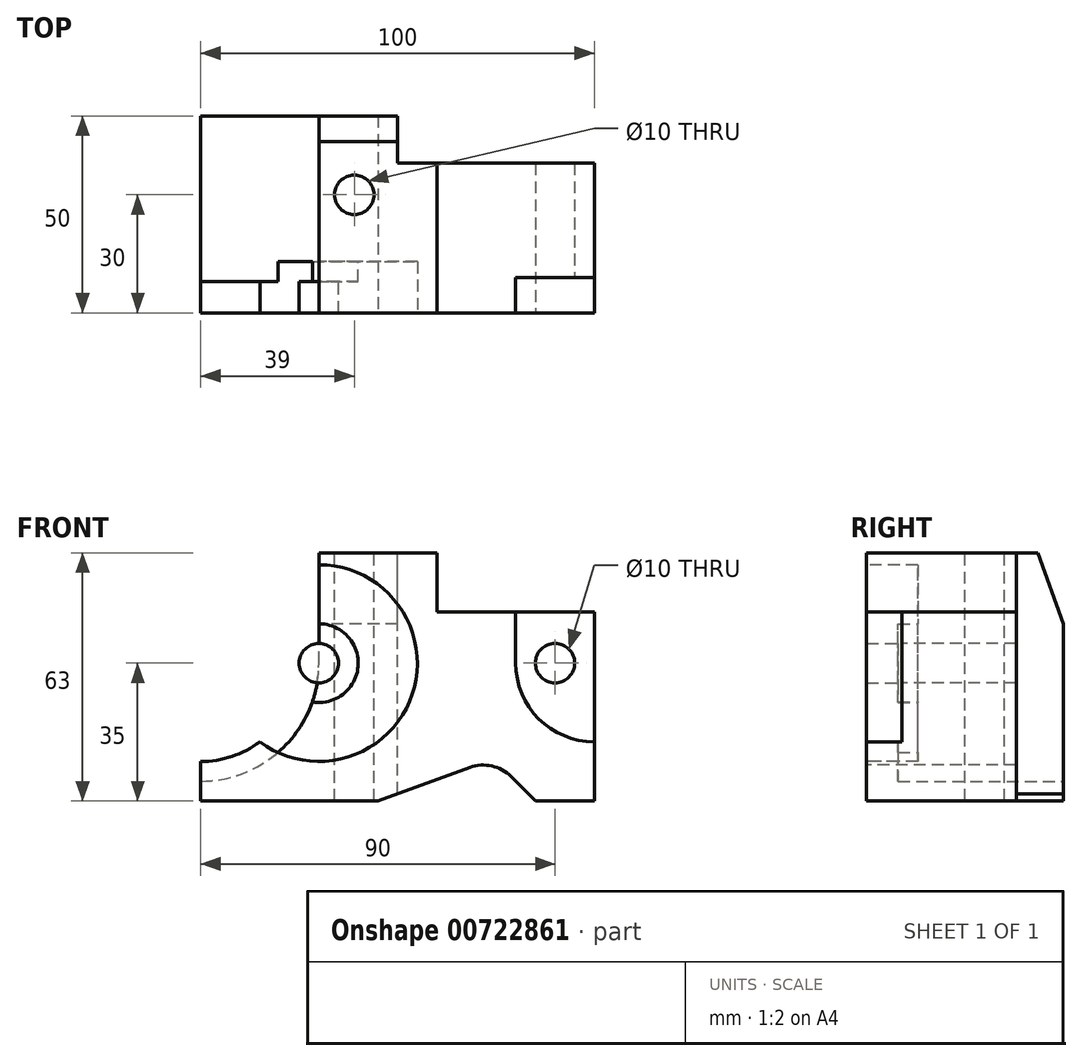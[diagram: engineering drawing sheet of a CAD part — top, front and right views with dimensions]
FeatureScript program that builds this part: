
annotation { "Feature Type Name" : "Feature", "Feature Type Description" : "" }
export const myFeature = defineFeature(function(context is Context, id is Id, definition is map)
    precondition{}
    {
        {
            var Q0;
            Q0=qCreatedBy(makeId("Front.planeOp"),FACE);
            var sketch = newSketch(context, id + "F0", { "sketchPlane" : qUnion([Q0])});
            skLineSegment(sketch, "E0", {"start": v(0, 0) * mm, "end": v(0, 63) * mm});
            skLineSegment(sketch, "E1", {"start": v(0, 0) * mm, "end": v(100, 0) * mm, "construction": true});
            skLineSegment(sketch, "E2", {"start": v(100, 0) * mm, "end": v(85, 0) * mm});
            skLineSegment(sketch, "E3", {"start": v(0, 0) * mm, "end": v(45, 0) * mm});
            skLineSegment(sketch, "E4", {"start": v(45, 0) * mm, "end": v(68.34, 8.5) * mm});
            skLineSegment(sketch, "E5", {"start": v(85, 0) * mm, "end": v(78.83, 6.17) * mm});
            skArc(sketch, "E6", {"start": v(78.83, 6.17) * mm, "mid": v(73.92, 8.86) * mm, "end": v(68.34, 8.5) * mm});
            skLineSegment(sketch, "E7", {"start": v(0, 63) * mm, "end": v(60, 63) * mm});
            skLineSegment(sketch, "E8", {"start": v(60, 63) * mm, "end": v(60, 48) * mm});
            skLineSegment(sketch, "E9", {"start": v(60, 48) * mm, "end": v(100, 48) * mm});
            skLineSegment(sketch, "E10", {"start": v(100, 48) * mm, "end": v(100, 0) * mm});
            skLineSegment(sketch, "E11", {"start": v(0, 35) * mm, "end": v(100, 35) * mm, "construction": true});
            skSolve(sketch);
        }
        {
            var Q0;
            Q0 = qSketchRegion(id + "F0", true);
            extrude(context, id + "F1", {"entities" : qUnion([Q0]), "oppositeDirection" : true, "depth" : 50 * mm, "offsetDistance" : 25 * mm});
        }
        {
            var Q0;
            Q0=makeQuery(id+"F1.opExtrude","CAP_FACE",FACE,{"disambiguationData":[OSD([sQuery(id+"F0.wireOp",EDGE,"E0"),sQuery(id+"F0.wireOp",EDGE,"E2"),sQuery(id+"F0.wireOp",EDGE,"E3"),sQuery(id+"F0.wireOp",EDGE,"E4"),sQuery(id+"F0.wireOp",EDGE,"E5"),sQuery(id+"F0.wireOp",EDGE,"E6"),sQuery(id+"F0.wireOp",EDGE,"E7"),sQuery(id+"F0.wireOp",EDGE,"E8"),sQuery(id+"F0.wireOp",EDGE,"E9"),sQuery(id+"F0.wireOp",EDGE,"E10")])],"isStart":true});
            var sketch = newSketch(context, id + "F2", { "sketchPlane" : qUnion([Q0])});
            skArc(sketch, "E12", {"start": v(80, 35) * mm, "mid": v(85.86, 20.86) * mm, "end": v(100, 15) * mm});
            skLineSegment(sketch, "E13", {"start": v(80, 35) * mm, "end": v(80, 48) * mm});
            skPoint(sketch, "E13.startSnap0", {"position": v(80, 48) * mm});
            skLineSegment(sketch, "E14", {"start": v(80, 48) * mm, "end": v(100, 48) * mm});
            skLineSegment(sketch, "E15", {"start": v(100, 48) * mm, "end": v(100, 15) * mm});
            skSolve(sketch);
        }
        {
            var Q0;
            Q0 = qSketchRegion(id + "F2", true);
            extrude(context, id + "F3", {"entities" : qUnion([Q0]), "operationType" : NewBodyOperationType.REMOVE, "oppositeDirection" : true, "depth" : 9 * mm, "offsetDistance" : 25 * mm});
        }
        {
            var Q0;
            Q0=makeQuery(id+"F3.boolean.opBoolean","COPY",FACE,{"derivedFrom":makeQuery(id+"F3.opExtrude","CAP_FACE",FACE,{"disambiguationData":[OSD([sQuery(id+"F2.wireOp",EDGE,"E12"),sQuery(id+"F2.wireOp",EDGE,"E13"),sQuery(id+"F2.wireOp",EDGE,"E14"),sQuery(id+"F2.wireOp",EDGE,"E15")])],"isStart":false})});
            var sketch = newSketch(context, id + "F4", { "sketchPlane" : qUnion([Q0])});
            skCircle(sketch, "E16", {"center": v(90, 35) * mm, "radius": 5 * mm});
            skSolve(sketch);
        }
        {
            var Q0;
            Q0 = qSketchRegion(id + "F4", true);
            extrude(context, id + "F5", {"entities" : qUnion([Q0]), "operationType" : NewBodyOperationType.REMOVE, "endBound" : BoundingType.THROUGH_ALL, "oppositeDirection" : true, "depth" : 25 * mm, "offsetDistance" : 25 * mm});
        }
        {
            var Q0;
            Q0=makeQuery(id+"F1.opExtrude","CAP_FACE",FACE,{"disambiguationData":[OSD([sQuery(id+"F0.wireOp",EDGE,"E0"),sQuery(id+"F0.wireOp",EDGE,"E2"),sQuery(id+"F0.wireOp",EDGE,"E3"),sQuery(id+"F0.wireOp",EDGE,"E4"),sQuery(id+"F0.wireOp",EDGE,"E5"),sQuery(id+"F0.wireOp",EDGE,"E6"),sQuery(id+"F0.wireOp",EDGE,"E7"),sQuery(id+"F0.wireOp",EDGE,"E8"),sQuery(id+"F0.wireOp",EDGE,"E9"),sQuery(id+"F0.wireOp",EDGE,"E10")])],"isStart":true});
            var sketch = newSketch(context, id + "F6", { "sketchPlane" : qUnion([Q0])});
            skLineSegment(sketch, "E17", {"start": v(0, 35) * mm, "end": v(80, 35) * mm, "construction": true});
            skCircle(sketch, "E18", {"center": v(30, 35) * mm, "radius": 25 * mm});
            skSolve(sketch);
        }
        {
            var Q0;
            Q0 = qSketchRegion(id + "F6", true);
            extrude(context, id + "F7", {"entities" : qUnion([Q0]), "operationType" : NewBodyOperationType.REMOVE, "oppositeDirection" : true, "depth" : 13 * mm, "offsetDistance" : 25 * mm});
        }
        {
            var Q0;
            Q0=makeQuery(id+"F7.boolean.opBoolean","COPY",FACE,{"derivedFrom":makeQuery(id+"F7.opExtrude","CAP_FACE",FACE,{"disambiguationData":[OSD([sQuery(id+"F6.wireOp",EDGE,"E18")])],"isStart":false})});
            var sketch = newSketch(context, id + "F8", { "sketchPlane" : qUnion([Q0])});
            skCircle(sketch, "E19", {"center": v(30, 35) * mm, "radius": 10 * mm});
            skSolve(sketch);
        }
        {
            var Q0;
            Q0 = qSketchRegion(id + "F8", true);
            extrude(context, id + "F9", {"entities" : qUnion([Q0]), "operationType" : NewBodyOperationType.ADD, "depth" : 5 * mm, "offsetDistance" : 25 * mm});
        }
        {
            var Q0;
            Q0=makeQuery(id+"F9.opExtrude","CAP_FACE",FACE,{"disambiguationData":[OSD([sQuery(id+"F8.wireOp",EDGE,"E19")])],"isStart":false});
            var sketch = newSketch(context, id + "F10", { "sketchPlane" : qUnion([Q0])});
            skCircle(sketch, "E20", {"center": v(30, 35) * mm, "radius": 5 * mm});
            skSolve(sketch);
        }
        {
            var Q0;
            Q0 = qSketchRegion(id + "F10", true);
            extrude(context, id + "F11", {"entities" : qUnion([Q0]), "operationType" : NewBodyOperationType.ADD, "depth" : 8 * mm, "offsetDistance" : 25 * mm});
        }
        {
            var Q0;
            Q0=makeQuery(id+"F1.opExtrude","CAP_FACE",FACE,{"disambiguationData":[OSD([sQuery(id+"F0.wireOp",EDGE,"E0"),sQuery(id+"F0.wireOp",EDGE,"E2"),sQuery(id+"F0.wireOp",EDGE,"E3"),sQuery(id+"F0.wireOp",EDGE,"E4"),sQuery(id+"F0.wireOp",EDGE,"E5"),sQuery(id+"F0.wireOp",EDGE,"E6"),sQuery(id+"F0.wireOp",EDGE,"E7"),sQuery(id+"F0.wireOp",EDGE,"E8"),sQuery(id+"F0.wireOp",EDGE,"E9"),sQuery(id+"F0.wireOp",EDGE,"E10")])],"isStart":true});
            var sketch = newSketch(context, id + "F12", { "sketchPlane" : qUnion([Q0])});
            skCircle(sketch, "E21", {"center": v(0, 35) * mm, "radius": 25 * mm});
            skSolve(sketch);
        }
        {
            var Q0;
            Q0 = qSketchRegion(id + "F12", true);
            extrude(context, id + "F13", {"entities" : qUnion([Q0]), "operationType" : NewBodyOperationType.REMOVE, "endBound" : BoundingType.THROUGH_ALL, "oppositeDirection" : true, "depth" : 25 * mm, "offsetDistance" : 25 * mm});
        }
        {
            var Q0;
            Q0=makeQuery(id+"F1.opExtrude","CAP_FACE",FACE,{"disambiguationData":[OSD([sQuery(id+"F0.wireOp",EDGE,"E0"),sQuery(id+"F0.wireOp",EDGE,"E2"),sQuery(id+"F0.wireOp",EDGE,"E3"),sQuery(id+"F0.wireOp",EDGE,"E4"),sQuery(id+"F0.wireOp",EDGE,"E5"),sQuery(id+"F0.wireOp",EDGE,"E6"),sQuery(id+"F0.wireOp",EDGE,"E7"),sQuery(id+"F0.wireOp",EDGE,"E8"),sQuery(id+"F0.wireOp",EDGE,"E9"),sQuery(id+"F0.wireOp",EDGE,"E10")])],"isStart":false});
            var sketch = newSketch(context, id + "F14", { "sketchPlane" : qUnion([Q0])});
            skLineSegment(sketch, "E22", {"start": v(0, 0) * mm, "end": v(0, 63) * mm, "construction": true});
            skLineSegment(sketch, "E23", {"start": v(0, 35) * mm, "end": v(-100, 35) * mm, "construction": true});
            skPoint(sketch, "E24.startSnap0", {"position": v(-30, 63) * mm});
            skArc(sketch, "E25", {"start": v(-30, 35) * mm, "mid": v(-21.21, 13.79) * mm, "end": v(0, 5) * mm});
            skLineSegment(sketch, "E26", {"start": v(-30, 35) * mm, "end": v(-30, 63) * mm});
            skLineSegment(sketch, "E27", {"start": v(0, 5) * mm, "end": v(0, 63) * mm});
            skLineSegment(sketch, "E28", {"start": v(0, 63) * mm, "end": v(-30, 63) * mm});
            skSolve(sketch);
        }
        {
            var Q0;
            Q0 = qSketchRegion(id + "F14", true);
            extrude(context, id + "F15", {"entities" : qUnion([Q0]), "operationType" : NewBodyOperationType.REMOVE, "oppositeDirection" : true, "depth" : 42 * mm, "offsetDistance" : 25 * mm});
        }
        {
            var Q0;
            {var subQ0=sQuery(id+"F14.wireOp",EDGE,"E26");Q0=makeQuery(id+"F15.boolean.opBoolean","COPY",FACE,{"disambiguationData":[TD([makeQuery(id+"F1.opExtrude","SWEPT_FACE",FACE,{"disambiguationData":[OSD([sQuery(id+"F0.wireOp",EDGE,"E0")])]}),makeQuery(id+"F1.opExtrude","SWEPT_FACE",FACE,{"disambiguationData":[OSD([sQuery(id+"F0.wireOp",EDGE,"E7")])]}),makeQuery(id+"F7.boolean.opBoolean","COPY",FACE,{"derivedFrom":makeQuery(id+"F7.opExtrude","SWEPT_FACE",FACE,{"disambiguationData":[OSD([sQuery(id+"F6.wireOp",EDGE,"E18")])]})}),makeQuery(id+"F13.boolean.opBoolean","COPY",FACE,{"derivedFrom":makeQuery(id+"F13.opExtrude","SWEPT_FACE",FACE,{"disambiguationData":[OSD([sQuery(id+"F12.wireOp",EDGE,"E21")])]})}),makeQuery(id+"F15.opExtrude","SWEPT_FACE",FACE,{"disambiguationData":[OSD([subQ0])]})])],"derivedFrom":makeQuery(id+"F15.opExtrude","CAP_FACE",FACE,{"disambiguationData":[OSD([sQuery(id+"F14.wireOp",EDGE,"E25"),subQ0,sQuery(id+"F14.wireOp",EDGE,"E27"),sQuery(id+"F14.wireOp",EDGE,"E28")])],"isStart":false})});}
            var sketch = newSketch(context, id + "F16", { "sketchPlane" : qUnion([Q0])});
            skLineSegment(sketch, "E29", {"start": v(-30, 63) * mm, "end": v(-30, 60) * mm});
            skSolve(sketch);
        }
        {
            var Q0;
            Q0 = qSketchRegion(id + "F16", true);
            var Q1;
            Q1=makeQuery(id+"F16.imprint","IMPRINT",FACE,{"disambiguationData":[TD([[makeQuery(id+"F16.imprint","IMPRINT",EDGE,{"derivedFrom":sQuery(id+"F16.wireOp",EDGE,"E29")}),-1.0]])]});
            extrude(context, id + "F17", {"entities" : qUnion([Q0, Q1]), "operationType" : NewBodyOperationType.REMOVE, "endBound" : BoundingType.THROUGH_ALL, "oppositeDirection" : true, "depth" : 25 * mm, "offsetDistance" : 25 * mm});
        }
        {
            var Q0;
            Q0=makeQuery(id+"F1.opExtrude","SWEPT_FACE",FACE,{"disambiguationData":[OSD([sQuery(id+"F0.wireOp",EDGE,"E3")])]});
            cPlane(context, id + "F18", {"entities" : qUnion([Q0]), "cplaneType" : CPlaneType.OFFSET, "offset" : 63 * mm, "oppositeDirection" : true, "width" : 150 * mm, "height" : 150 * mm});
        }
        {
            var Q0;
            Q0=qCreatedBy(id+"F18.planeOp",FACE);
            var sketch = newSketch(context, id + "F19", { "sketchPlane" : qUnion([Q0])});
            skLineSegment(sketch, "E30.0.3", {"start": v(60, -50) * mm, "end": v(50, -50) * mm});
            skLineSegment(sketch, "E31.0.2", {"start": v(100, -38) * mm, "end": v(100, -50) * mm});
            skLineSegment(sketch, "E31.0.3", {"start": v(100, -50) * mm, "end": v(60, -50) * mm});
            skLineSegment(sketch, "E32", {"start": v(50, -50) * mm, "end": v(50, -38) * mm});
            skLineSegment(sketch, "E33", {"start": v(50, -38) * mm, "end": v(100, -38) * mm});
            skPoint(sketch, "E31.0.1.end.orphan", {"position": v(100, -9) * mm});
            skPoint(sketch, "E31.0.0.end.orphan", {"position": v(80, -9) * mm});
            skPoint(sketch, "E31.0.5.end.orphan", {"position": v(80, 0) * mm});
            skPoint(sketch, "E34.orphan", {"position": v(60, 0) * mm});
            skPoint(sketch, "E30.0.0.end.orphan", {"position": v(30, 0) * mm});
            skPoint(sketch, "E35.orphan", {"position": v(30, -50) * mm});
            skSolve(sketch);
        }
        {
            var Q0;
            Q0 = qSketchRegion(id + "F19", true);
            extrude(context, id + "F20", {"entities" : qUnion([Q0]), "operationType" : NewBodyOperationType.REMOVE, "endBound" : BoundingType.THROUGH_ALL, "depth" : 25 * mm, "offsetDistance" : 25 * mm});
        }
        {
            var Q0;
            Q0=makeQuery(id+"F17.boolean.opBoolean","MERGE",FACE,{"derivedFrom":[makeQuery(id+"F15.boolean.opBoolean","COPY",FACE,{"derivedFrom":makeQuery(id+"F15.opExtrude","SWEPT_FACE",FACE,{"disambiguationData":[OSD([sQuery(id+"F14.wireOp",EDGE,"E26")])]})}),makeQuery(id+"F17.opExtrude","SWEPT_FACE",FACE,{"disambiguationData":[OSD([sQuery(id+"F16.wireOp",EDGE,"E29")])]})]});
            var sketch = newSketch(context, id + "F21", { "sketchPlane" : qUnion([Q0])});
            skLineSegment(sketch, "E36", {"start": v(-50, 63) * mm, "end": v(-50, 45) * mm});
            skLineSegment(sketch, "E37", {"start": v(-50, 45) * mm, "end": v(-43.45, 63) * mm});
            skLineSegment(sketch, "E38", {"start": v(-50, 63) * mm, "end": v(-43.45, 63) * mm});
            skSolve(sketch);
        }
        {
            var Q0;
            Q0 = qSketchRegion(id + "F21", true);
            extrude(context, id + "F22", {"entities" : qUnion([Q0]), "operationType" : NewBodyOperationType.REMOVE, "endBound" : BoundingType.THROUGH_ALL, "oppositeDirection" : true, "depth" : 25 * mm, "offsetDistance" : 25 * mm});
        }
        {
            var Q0;
            Q0=makeQuery(id+"F1.opExtrude","SWEPT_FACE",FACE,{"disambiguationData":[OSD([sQuery(id+"F0.wireOp",EDGE,"E7")])]});
            var sketch = newSketch(context, id + "F23", { "sketchPlane" : qUnion([Q0])});
            skCircle(sketch, "E39", {"center": v(39, 30) * mm, "radius": 5 * mm});
            skSolve(sketch);
        }
        {
            var Q0;
            Q0 = qSketchRegion(id + "F23", true);
            extrude(context, id + "F24", {"entities" : qUnion([Q0]), "operationType" : NewBodyOperationType.REMOVE, "endBound" : BoundingType.THROUGH_ALL, "oppositeDirection" : true, "depth" : 25 * mm, "offsetDistance" : 25 * mm});
        }
    });
